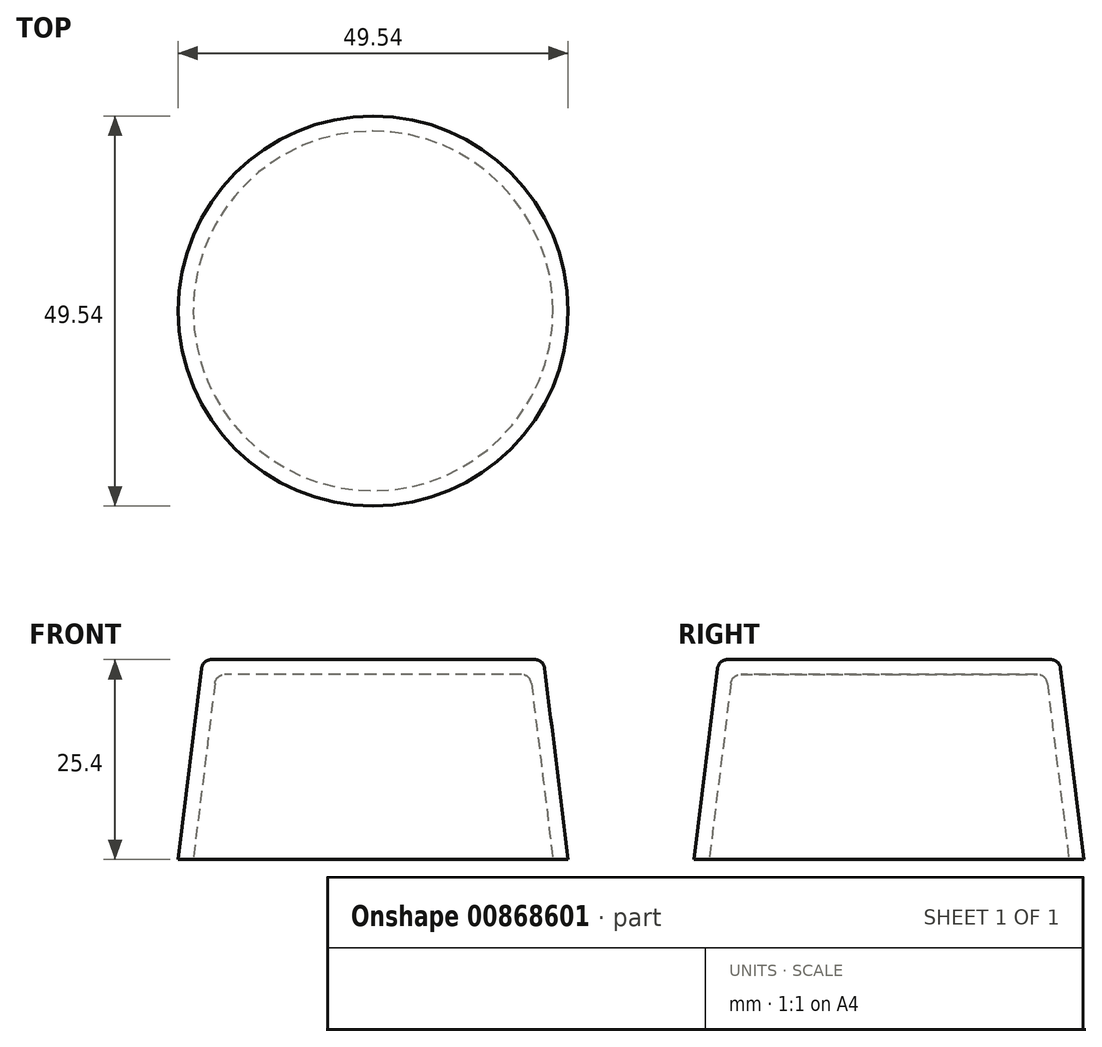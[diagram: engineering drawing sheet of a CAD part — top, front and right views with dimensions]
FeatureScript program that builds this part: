
annotation { "Feature Type Name" : "Feature", "Feature Type Description" : "" }
export const myFeature = defineFeature(function(context is Context, id is Id, definition is map)
    precondition{}
    {
        {
            var Q0;
            Q0=qCreatedBy(makeId("Top.planeOp"),FACE);
            var sketch = newSketch(context, id + "F0", { "sketchPlane" : qUnion([Q0])});
            skCircle(sketch, "E0.0", {"center": v(0, 0) * mm, "radius": 24.77 * mm});
            skSolve(sketch);
        }
        {
            var Q0;
            Q0=makeQuery(id+"F0.imprint","IMPRINT",FACE,{"disambiguationData":[TD([[makeQuery(id+"F0.imprint","IMPRINT",EDGE,{"derivedFrom":sQuery(id+"F0.wireOp",EDGE,"E0.0")}),1.0]])]});
            extrude(context, id + "F1", {"entities" : qUnion([Q0]), "depth" : 25.4 * mm, "offsetDistance" : 25.4 * mm, "hasDraft" : true, "draftAngle" : 7 * degree, "draftPullDirection" : true});
        }
        {
            var Q0;
            Q0=makeQuery(id+"F1.opExtrude","CAP_FACE",FACE,{"disambiguationData":[OSD([sQuery(id+"F0.wireOp",EDGE,"E0.0")])],"isStart":true});
            shell(context, id + "F2", {"entities" : qUnion([Q0]), "thickness" : 1.9 * mm});
        }
        {
            var Q0;
            {var subQ0=sQuery(id+"F0.wireOp",EDGE,"E0.0");Q0=makeQuery(id+"F2.opShell","OFFSET_EDGE",EDGE,{"disambiguationData":[OSD([subQ0]),TDD([makeQuery(id+"F1.opExtrude","CAP_EDGE",EDGE,{"disambiguationData":[OSD([subQ0])],"isStart":false})])]});}
            var Q1;
            Q1=makeQuery(id+"F1.opExtrude","CAP_EDGE",EDGE,{"disambiguationData":[OSD([sQuery(id+"F0.wireOp",EDGE,"E0.0")])],"isStart":false});
            fillet(context, id + "F3", {"entities" : qUnion([Q0, Q1]), "radius" : 1.27 * mm, "tangentPropagation" : true, "allowEdgeOverflow" : false});
        }
    });
